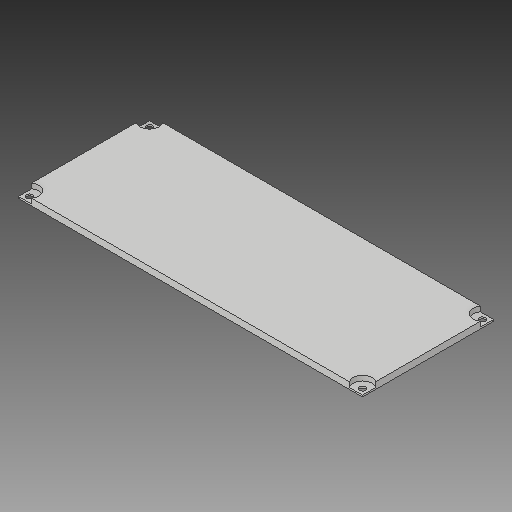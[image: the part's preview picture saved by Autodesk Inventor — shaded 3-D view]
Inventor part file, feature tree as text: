
AUTODESK INVENTOR PART (.ipt)
format: ipt  version: 2018 (Build 220112000, 112)  size: 152,064 bytes
history: native  units: in
note: dims shown in document units (in); Inventor stores cm internally (conversion verified against a paired STEP export)
features: extrude x4, sketch x4
ambient origin geometry x8: Origin, YZ Plane, XZ Plane, XY Plane, X Axis, Y Axis, Z Axis, Center Point
bodies: Solid1 (feature_tree)
feature tree (8):
  extrude  "Extrusion1"  Depth=2.5in
  extrude  "Extrusion2"  Depth=0.125in
  extrude  "Extrusion3"  Depth=0.1181in
  extrude  "Extrusion4"  Depth=0.0938in
  sketch  "Sketch1"  dims[d0=6.5in d1=2.5in]
  sketch  "Sketch2"  dims[d2=0.125in d3=0.0in d4=0.25in]
  sketch  "Sketch3"  dims[d5=0.25in d6=0.1181in]
  sketch  "Sketch4"  dims[d7=0.1181in d8=0.1181in d9=0.1181in d10=0.125in d11=0.0in d12=0.3543in d13=0.3543in d14=0.3543in d15=0.3543in d16=0.0938in d17=0.0in d18=0.0197in d19=0.0197in d20=1.0in d21=0.0in]
